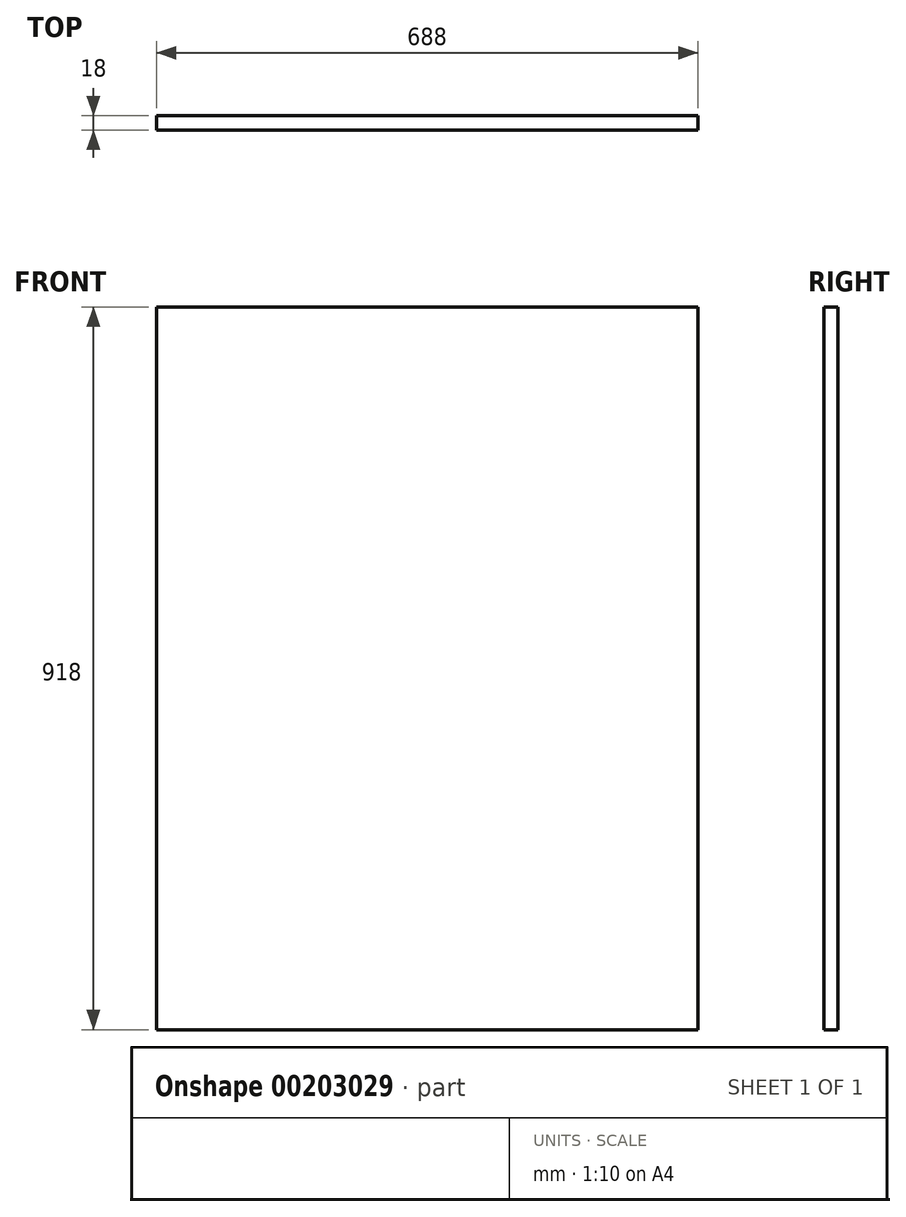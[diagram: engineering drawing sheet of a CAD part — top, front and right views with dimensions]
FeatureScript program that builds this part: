
annotation { "Feature Type Name" : "Feature", "Feature Type Description" : "" }
export const myFeature = defineFeature(function(context is Context, id is Id, definition is map)
    precondition{}
    {
        {
            var Q0;
            Q0=qCreatedBy(makeId("Front.planeOp"),FACE);
            var sketch = newSketch(context, id + "F0", { "sketchPlane" : qUnion([Q0])});
            skLineSegment(sketch, "E0.bottom", {"start": v(-344, -459) * mm, "end": v(344, -459) * mm});
            skLineSegment(sketch, "E0.top", {"start": v(-344, 459) * mm, "end": v(344, 459) * mm});
            skLineSegment(sketch, "E0.left", {"start": v(-344, -459) * mm, "end": v(-344, 459) * mm});
            skLineSegment(sketch, "E0.right", {"start": v(344, -459) * mm, "end": v(344, 459) * mm});
            skPoint(sketch, "E0.middle", {"position": v(0, 0) * mm});
            skSolve(sketch);
        }
        {
            var Q0;
            Q0=makeQuery(id+"F0.imprint","IMPRINT",FACE,{"disambiguationData":[TD([[makeQuery(id+"F0.imprint","IMPRINT",EDGE,{"derivedFrom":sQuery(id+"F0.wireOp",EDGE,"E0.bottom")}),1.0]])]});
            extrude(context, id + "F1", {"entities" : qUnion([Q0]), "depth" : 18 * mm});
        }
    });
